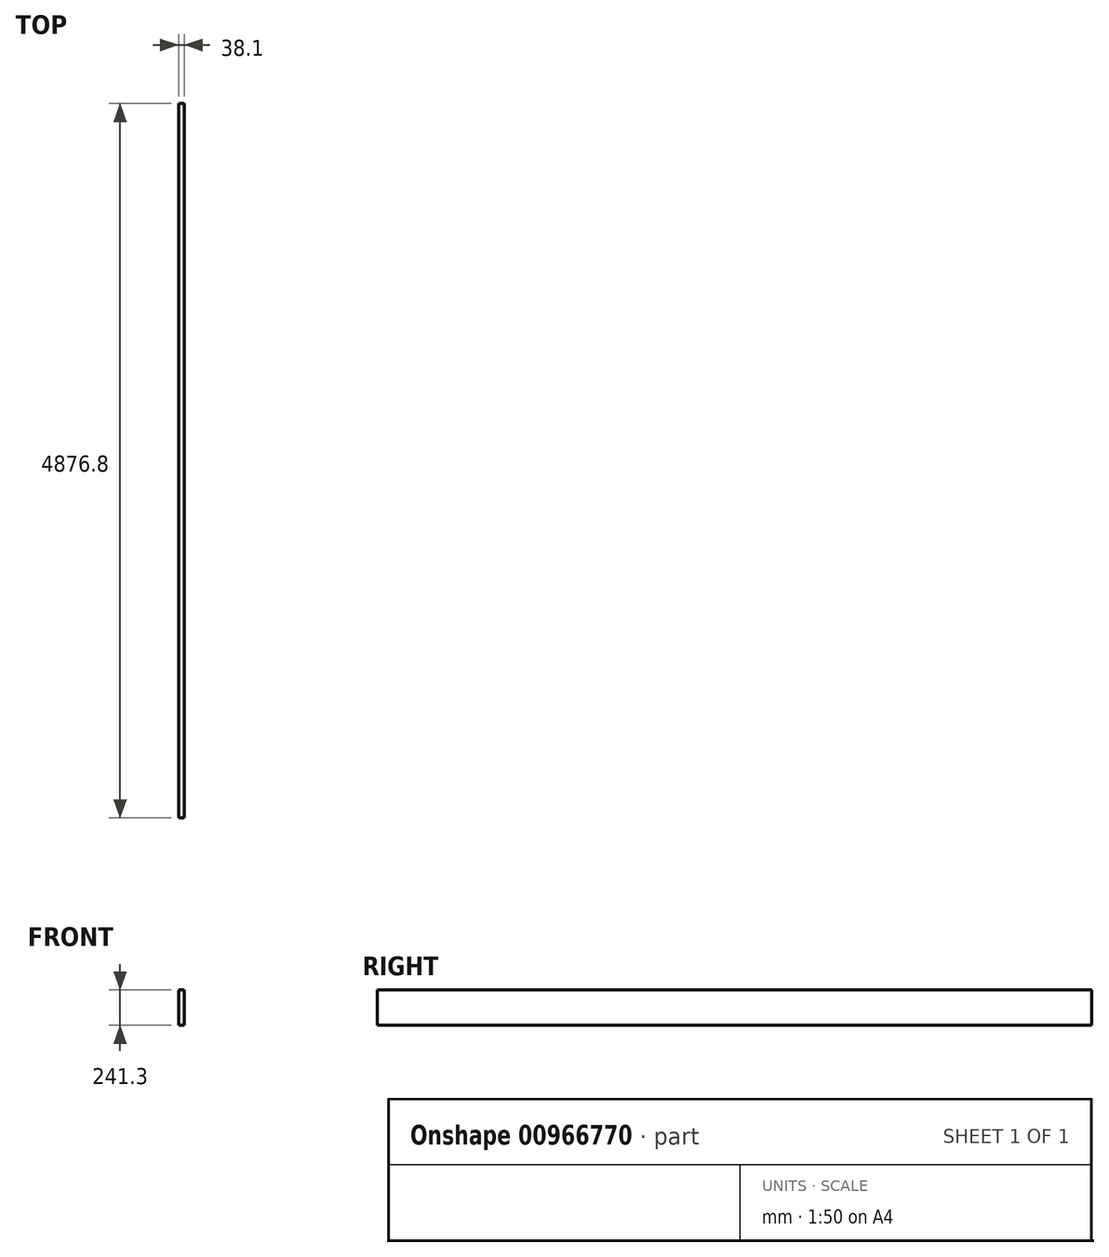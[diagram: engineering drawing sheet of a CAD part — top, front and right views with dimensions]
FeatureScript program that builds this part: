
annotation { "Feature Type Name" : "Feature", "Feature Type Description" : "" }
export const myFeature = defineFeature(function(context is Context, id is Id, definition is map)
    precondition{}
    {
        {
            var Q0;
            Q0=qCreatedBy(makeId("Front.planeOp"),FACE);
            var sketch = newSketch(context, id + "F0", { "sketchPlane" : qUnion([Q0])});
            skLineSegment(sketch, "E0.bottom", {"start": v(0, 0) * mm, "end": v(38.1, 0) * mm});
            skLineSegment(sketch, "E0.top", {"start": v(0, 241.3) * mm, "end": v(38.1, 241.3) * mm});
            skLineSegment(sketch, "E0.left", {"start": v(0, 0) * mm, "end": v(0, 241.3) * mm});
            skLineSegment(sketch, "E0.right", {"start": v(38.1, 0) * mm, "end": v(38.1, 241.3) * mm});
            skSolve(sketch);
        }
        {
            var Q0;
            Q0=makeQuery(id+"F0.imprint","IMPRINT",FACE,{"disambiguationData":[TD([[makeQuery(id+"F0.imprint","IMPRINT",EDGE,{"derivedFrom":sQuery(id+"F0.wireOp",EDGE,"E0.bottom")}),1.0]])]});
            extrude(context, id + "F1", {"entities" : qUnion([Q0]), "depth" : 4876.8 * mm, "offsetDistance" : 25.4 * mm});
        }
    });
